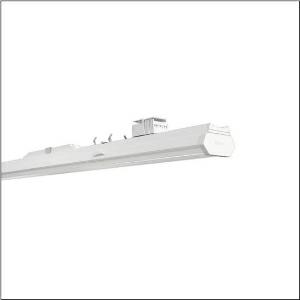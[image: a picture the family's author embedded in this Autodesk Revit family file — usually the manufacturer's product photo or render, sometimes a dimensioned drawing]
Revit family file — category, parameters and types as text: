
# Revit family: licross_r__21_protected_mo_52td12dn4a5g3s4_b622
name_source: partatom
category: Lighting Fixtures
units: mm (PartAtom-declared; Revit-internal decimal feet)

## family parameters
Cut with Voids When Loaded = No
Host = Face
Light Source = No
Part Type = Normal
Room Calculation Point = No
Round Connector Dimension = Use Diameter
Shared = No

## types (1)
- --- (1 x LED, 940 lm, 6.8 W, 4000K)
    Apparent Load = 7 VA
    CIE Flux Codes = 73 92 98 99 100
    Color Rendering = 80
    Color Temperature = 4000K
    Default Elevation = 1800 mm
    Description = Licross® 21 Protected MO, luminaire insert, of sheet steel, galvanised, coil coated, white, length: 1.500mm, width: 90mm, height: 103mm, LED rated luminous flux: 10.700lm, light colour: 840, control gear: DALI 2, with plug, 6-pole, with phase selection, for trunking rail, 9 or 11-core, mains connection: 220..240V, AC, 50/60Hz, rated input power: 66W, for trunking rail, 9-/11-core, halogen-free wiring, for emergency light function, converter,control gear: single battery element, battery: LiFePO4, 9Ah, primary light control with lens, of plastic, primary optical cover: cover, of PMMA, light emission: direct distribution, primary light characteristic: symmetric, protection rating (complete): IP54, insulation class (complete): insulation class I (protective earthing), certification: CE, UKCA, protection symbol: D if used in an environment with non-conductive dust loads with corresponding accessories, impact resistance: IK06, permissible ambient temperature for indoor applications: +5..+35°C, standard: EN 60598-2-22, LABS conformity tested according to VDMA 24364:2018-05, reducing of maximum allowable ambient temperature of 5°C with ceiling mounting, corresponds to IFS (International Featured Standards) requirements for safety and quality in the food industry, packaging unit: 1 piece
    Height = 92 mm
    Lamp = 1 x LED
    Lamp Light Flux = 940 lm
    Lamp Power = 6.8 W
    Lamp count = 1
    Length = 1500 mm
    Luminous efficacy = 138 lm/W
    Manufacturer = Siteco
    ModVariant = No
    Model = 52TD12DN4A5G3S4
    Mounting Place = Ceiling
    Mounting Type = Pendant
    Number of Poles = 1
    OnlyDefault = Yes
    Power Factor = 1
    Product Name = Licross® 21 Protected MO
    Product group = luminaire insert
    ProductGroupID = 902
    Protection Class = Protection class I
    Protection Degree = IP 54
    RLX_Detail_Level = 1
    RLX_Emergency_Light_Flux = 0 lm
    RLX_Emergency_Type = 0
    RLX_Emergency_Type_DB = No
    RlxData = <blob elided: 24869 chars, md5=fd574351>
    Socket = socket
    Standby Power = 0 W
    System Light Flux = 940 lm
    System Power = 7 W
    Type Comments = : emergency light operation: 3 h
    Type Image = l_1256148.jpg
    URL = http://relux.com
    VarID = @adj_110928
    Voltage = 0 V
    Weight = 0.00 kg
    Width = 88 mm

## geometry (parser evidence)
native form markers: Blend x4, Sweep x10
no freeform markers — native parametric forms only
